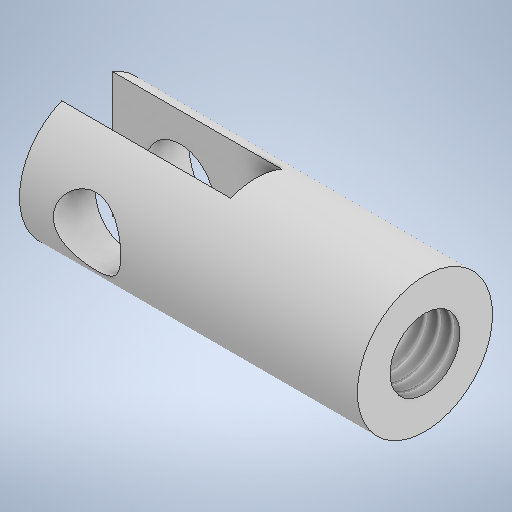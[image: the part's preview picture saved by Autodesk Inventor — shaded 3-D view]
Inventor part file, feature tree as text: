
AUTODESK INVENTOR PART (.ipt)
format: ipt  version: 2025.1 (Build 291241000, 241)  size: 269,312 bytes
history: native  units: mm
features: sketch x4, plane x2, hole x2, revolve x1, extrude x1, projected_geometry x1
ambient origin geometry x8: Origin, YZ Plane, XZ Plane, XY Plane, X Axis, Y Axis, Z Axis, Center Point
bodies: Solid1 (feature_tree)
feature tree (11):
  revolve  "Revolution1"  [1 undecoded]
  plane  "Work Plane1"
  plane  "Work Plane3"
  extrude  "Extrusion1"  Depth=4.0mm
  hole  "Hole2"  [1 undecoded]
  hole  "Hole3"  [1 undecoded]
  sketch  "Sketch1"  dims[d0=8.0mm d1=20.0mm]
  sketch  "Sketch2"  dims[d2=90.0deg d3=4.0mm]
  projected_geometry  "Projected Loop1"
  sketch  "Sketch4"  dims[d4=10.0mm d5=3.0mm]
  sketch  "Sketch5"  dims[d6=8.0mm d7=0.0mm d17=4.0mm d18=16.0mm d19=4.0mm d20=6.0mm d21=4.0mm d22=2.0mm d23=90.0deg d24=8.0mm d25=0.0mm d26=4.134mm d27=8.0mm d28=4.0mm d29=2.0mm d30=90.0deg d31=8.0mm d32=0.0mm]
note: 3 required parameter values undecoded (feature->parameter linkage not recoverable at this tier; creation-order binding heuristic only, values carry confidence <= 0.55)